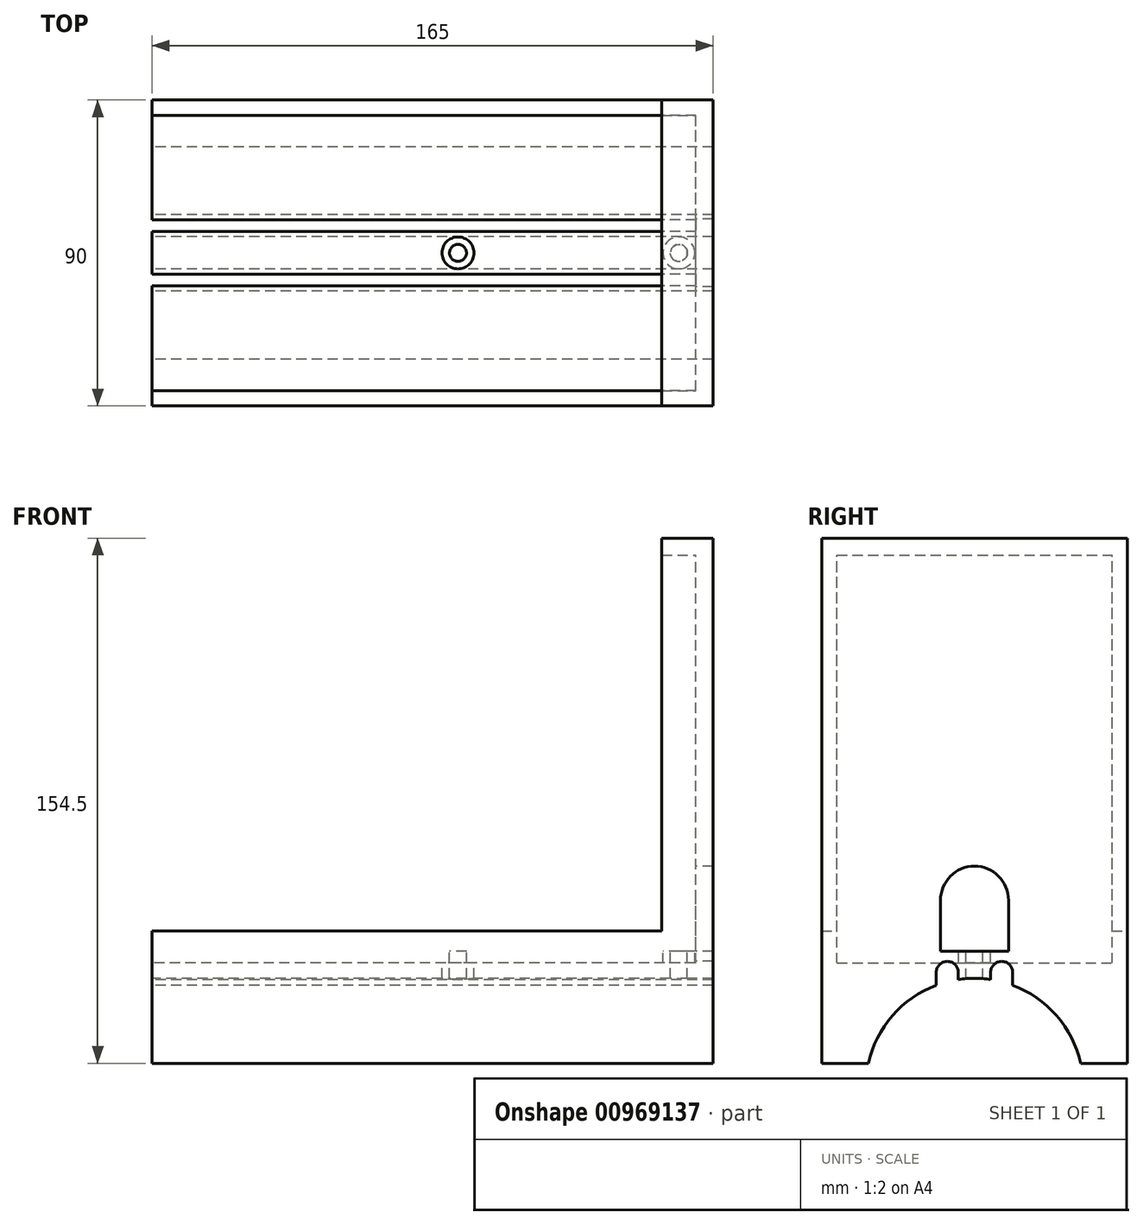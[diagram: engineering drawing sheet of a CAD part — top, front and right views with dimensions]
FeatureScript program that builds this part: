
annotation { "Feature Type Name" : "Feature", "Feature Type Description" : "" }
export const myFeature = defineFeature(function(context is Context, id is Id, definition is map)
    precondition{}
    {
        {
            var Q0;
            Q0=qCreatedBy(makeId("Right.planeOp"),FACE);
            var sketch = newSketch(context, id + "F0", { "sketchPlane" : qUnion([Q0])});
            skLineSegment(sketch, "E0", {"start": v(0, 25) * mm, "end": v(0, 89.87) * mm});
            skLineSegment(sketch, "E1", {"start": v(-31.25, 0) * mm, "end": v(-45, 0) * mm});
            skLineSegment(sketch, "E2.MirrorCS", {"start": v(31.25, 0) * mm, "end": v(45, 0) * mm});
            skArc(sketch, "E3", {"start": v(31.25, 0) * mm, "mid": v(24.15, 14) * mm, "end": v(11.25, 22.96) * mm});
            skPoint(sketch, "E4.orphan", {"position": v(0, 0) * mm});
            skLineSegment(sketch, "E5.0", {"start": v(11.25, 22.96) * mm, "end": v(11.25, 26.75) * mm});
            skLineSegment(sketch, "E6.MirrorCS", {"start": v(4.75, 24.65) * mm, "end": v(4.75, 26.75) * mm});
            skArc(sketch, "E7.trimOffspring", {"start": v(11.25, 26.75) * mm, "mid": v(8, 30) * mm, "end": v(4.75, 26.75) * mm});
            skArc(sketch, "E8.trimOffspring", {"start": v(4.75, 24.65) * mm, "mid": v(0, 25) * mm, "end": v(-4.75, 24.65) * mm});
            skLineSegment(sketch, "E9.MirrorCS", {"start": v(-4.75, 24.65) * mm, "end": v(-4.75, 26.75) * mm});
            skArc(sketch, "E10.MirrorCS", {"start": v(-11.25, 26.75) * mm, "mid": v(-8, 30) * mm, "end": v(-4.75, 26.75) * mm});
            skLineSegment(sketch, "E11.MirrorCS", {"start": v(-11.25, 22.96) * mm, "end": v(-11.25, 26.75) * mm});
            skArc(sketch, "E12.trimOffspring", {"start": v(-11.25, 22.96) * mm, "mid": v(-24.15, 14) * mm, "end": v(-31.25, 0) * mm});
            skPoint(sketch, "E13.orphan", {"position": v(-31.25, 89.87) * mm});
            skPoint(sketch, "E14.orphan", {"position": v(31.25, 89.87) * mm});
            skPoint(sketch, "E15.orphan", {"position": v(-123.78, 0) * mm});
            skPoint(sketch, "E16.orphan", {"position": v(123.78, 0) * mm});
            skLineSegment(sketch, "E17.0", {"start": v(-45, 0) * mm, "end": v(-45, 39) * mm});
            skLineSegment(sketch, "E18.0", {"start": v(45, 0) * mm, "end": v(45, 39) * mm});
            skLineSegment(sketch, "E19.0", {"start": v(-45, 39) * mm, "end": v(-40.5, 39) * mm});
            skLineSegment(sketch, "E20.0", {"start": v(-40.5, 33) * mm, "end": v(-40.5, 39) * mm});
            skLineSegment(sketch, "E21.trimOffspring", {"start": v(0, 33) * mm, "end": v(40.5, 33) * mm});
            skLineSegment(sketch, "E22", {"start": v(-40.5, 33) * mm, "end": v(0, 33) * mm});
            skLineSegment(sketch, "E23.trimOffspring", {"start": v(40.5, 39) * mm, "end": v(45, 39) * mm});
            skLineSegment(sketch, "E24.MirrorCS", {"start": v(40.5, 33) * mm, "end": v(40.5, 39) * mm});
            skSolve(sketch);
        }
        {
            var Q0;
            Q0 = qSketchRegion(id + "F0", true);
            extrude(context, id + "F1", {"entities" : qUnion([Q0]), "depth" : 160 * mm, "offsetDistance" : 25 * mm});
        }
        {
            var Q0;
            Q0=makeQuery(id+"F1.opExtrude","CAP_FACE",FACE,{"disambiguationData":[OSD([sQuery(id+"F0.wireOp",EDGE,"E1"),sQuery(id+"F0.wireOp",EDGE,"E2.MirrorCS"),sQuery(id+"F0.wireOp",EDGE,"E3"),sQuery(id+"F0.wireOp",EDGE,"E5.0"),sQuery(id+"F0.wireOp",EDGE,"E6.MirrorCS"),sQuery(id+"F0.wireOp",EDGE,"E7.trimOffspring"),sQuery(id+"F0.wireOp",EDGE,"E8.trimOffspring"),sQuery(id+"F0.wireOp",EDGE,"E9.MirrorCS"),sQuery(id+"F0.wireOp",EDGE,"E10.MirrorCS"),sQuery(id+"F0.wireOp",EDGE,"E11.MirrorCS"),sQuery(id+"F0.wireOp",EDGE,"E12.trimOffspring"),sQuery(id+"F0.wireOp",EDGE,"E17.0"),sQuery(id+"F0.wireOp",EDGE,"E18.0"),sQuery(id+"F0.wireOp",EDGE,"E19.0"),sQuery(id+"F0.wireOp",EDGE,"E20.0"),sQuery(id+"F0.wireOp",EDGE,"E21.trimOffspring"),sQuery(id+"F0.wireOp",EDGE,"E22"),sQuery(id+"F0.wireOp",EDGE,"E23.trimOffspring"),sQuery(id+"F0.wireOp",EDGE,"E24.MirrorCS")])],"isStart":false});
            var sketch = newSketch(context, id + "F2", { "sketchPlane" : qUnion([Q0])});
            skLineSegment(sketch, "E25.0.5", {"start": v(31.25, 0) * mm, "end": v(45, 0) * mm});
            skLineSegment(sketch, "E25.0.6", {"start": v(45, 0) * mm, "end": v(45, 149.5) * mm});
            skLineSegment(sketch, "E25.0.12", {"start": v(-45, 149.5) * mm, "end": v(-45, 0) * mm});
            skLineSegment(sketch, "E25.0.13", {"start": v(-45, 0) * mm, "end": v(-31.25, 0) * mm});
            skLineSegment(sketch, "E26.0", {"start": v(-45, 149.5) * mm, "end": v(45, 149.5) * mm});
            skPoint(sketch, "E27.orphan", {"position": v(-45, 39) * mm});
            skPoint(sketch, "E28.orphan", {"position": v(45, 39) * mm});
            skArc(sketch, "E29.0.0", {"start": v(-4.75, 24.65) * mm, "mid": v(0, 25) * mm, "end": v(4.75, 24.65) * mm});
            skLineSegment(sketch, "E29.0.1", {"start": v(4.75, 24.65) * mm, "end": v(4.75, 26.75) * mm});
            skArc(sketch, "E29.0.2", {"start": v(4.75, 26.75) * mm, "mid": v(8, 30) * mm, "end": v(11.25, 26.75) * mm});
            skLineSegment(sketch, "E29.0.3", {"start": v(11.25, 26.75) * mm, "end": v(11.25, 22.96) * mm});
            skArc(sketch, "E29.0.4", {"start": v(11.25, 22.96) * mm, "mid": v(24.15, 14) * mm, "end": v(31.25, 0) * mm});
            skLineSegment(sketch, "E29.0.6", {"start": v(45, 0) * mm, "end": v(45, 39) * mm});
            skLineSegment(sketch, "E29.0.7", {"start": v(45, 39) * mm, "end": v(40.5, 39) * mm});
            skLineSegment(sketch, "E29.0.8", {"start": v(40.5, 39) * mm, "end": v(40.5, 33) * mm});
            skLineSegment(sketch, "E29.0.9", {"start": v(40.5, 33) * mm, "end": v(-40.5, 33) * mm});
            skLineSegment(sketch, "E29.0.10", {"start": v(-40.5, 33) * mm, "end": v(-40.5, 39) * mm});
            skLineSegment(sketch, "E29.0.11", {"start": v(-40.5, 39) * mm, "end": v(-45, 39) * mm});
            skLineSegment(sketch, "E29.0.12", {"start": v(-45, 39) * mm, "end": v(-45, 0) * mm});
            skArc(sketch, "E29.0.14", {"start": v(-31.25, 0) * mm, "mid": v(-24.15, 14) * mm, "end": v(-11.25, 22.96) * mm});
            skLineSegment(sketch, "E29.0.15", {"start": v(-11.25, 22.96) * mm, "end": v(-11.25, 26.75) * mm});
            skArc(sketch, "E29.0.16", {"start": v(-11.25, 26.75) * mm, "mid": v(-8, 30) * mm, "end": v(-4.75, 26.75) * mm});
            skLineSegment(sketch, "E29.0.17", {"start": v(-4.75, 26.75) * mm, "end": v(-4.75, 24.65) * mm});
            skSolve(sketch);
        }
        {
            var Q0;
            Q0 = qSketchRegion(id + "F2", true);
            extrude(context, id + "F3", {"entities" : qUnion([Q0]), "operationType" : NewBodyOperationType.ADD, "depth" : 5 * mm, "offsetDistance" : 25 * mm});
        }
        {
            var Q0;
            {var subQ0=sQuery(id+"F2.wireOp",EDGE,"E25.0.12");var subQ1=sQuery(id+"F2.wireOp",EDGE,"E25.0.6");var subQ2=sQuery(id+"F2.wireOp",EDGE,"E26.0");Q0=makeQuery(id+"F3.boolean.opBoolean","SPLIT",FACE,{"disambiguationData":[TD([makeQuery(id+"F1.opExtrude","SWEPT_FACE",FACE,{"disambiguationData":[OSD([sQuery(id+"F0.wireOp",EDGE,"E17.0")])]})])],"derivedFrom":makeQuery(id+"F3.opExtrude","CAP_FACE",FACE,{"disambiguationData":[OSD([sQuery(id+"F2.wireOp",EDGE,"E25.0.5"),subQ1,subQ0,sQuery(id+"F2.wireOp",EDGE,"E25.0.13"),subQ2])],"isStart":true})});}
            var sketch = newSketch(context, id + "F4", { "sketchPlane" : qUnion([Q0])});
            skLineSegment(sketch, "E30.0", {"start": v(-40.5, 39) * mm, "end": v(-45, 39) * mm});
            skLineSegment(sketch, "E31", {"start": v(-45, 39) * mm, "end": v(-45, 149.5) * mm});
            skLineSegment(sketch, "E32", {"start": v(-40.5, 39) * mm, "end": v(-40.5, 149.5) * mm});
            skPoint(sketch, "E33.orphan", {"position": v(45, 149.5) * mm});
            skLineSegment(sketch, "E34.0", {"start": v(45, 39) * mm, "end": v(40.5, 39) * mm});
            skLineSegment(sketch, "E35.0", {"start": v(45, 149.5) * mm, "end": v(45, 39) * mm});
            skLineSegment(sketch, "E36", {"start": v(40.5, 39) * mm, "end": v(40.5, 149.5) * mm});
            skLineSegment(sketch, "E37.0", {"start": v(-40.5, 149.5) * mm, "end": v(-45, 149.5) * mm});
            skLineSegment(sketch, "E38.0", {"start": v(45, 149.5) * mm, "end": v(40.5, 149.5) * mm});
            skPoint(sketch, "E39.orphan", {"position": v(-45, 149.5) * mm});
            skSolve(sketch);
        }
        {
            var Q0;
            Q0 = qSketchRegion(id + "F4", true);
            extrude(context, id + "F5", {"entities" : qUnion([Q0]), "operationType" : NewBodyOperationType.ADD, "depth" : 10 * mm, "offsetDistance" : 25 * mm});
        }
        {
            var Q0;
            Q0=makeQuery(id+"F5.boolean.opBoolean","MERGE",FACE,{"derivedFrom":[makeQuery(id+"F3.opExtrude","SWEPT_FACE",FACE,{"disambiguationData":[OSD([sQuery(id+"F2.wireOp",EDGE,"E26.0")])]}),makeQuery(id+"F5.opExtrude","SWEPT_FACE",FACE,{"disambiguationData":[OSD([sQuery(id+"F4.wireOp",EDGE,"E37.0")])]}),makeQuery(id+"F5.opExtrude","SWEPT_FACE",FACE,{"disambiguationData":[OSD([sQuery(id+"F4.wireOp",EDGE,"E38.0")])]})]});
            var sketch = newSketch(context, id + "F6", { "sketchPlane" : qUnion([Q0])});
            skLineSegment(sketch, "E40.0.3", {"start": v(150, -45) * mm, "end": v(165, -45) * mm});
            skLineSegment(sketch, "E40.0.4", {"start": v(165, -45) * mm, "end": v(165, 45) * mm});
            skLineSegment(sketch, "E40.0.5", {"start": v(165, 45) * mm, "end": v(150, 45) * mm});
            skLineSegment(sketch, "E40.0.6", {"start": v(150, 45) * mm, "end": v(150, -45) * mm});
            skPoint(sketch, "E41.orphan", {"position": v(150, 40.5) * mm});
            skLineSegment(sketch, "E42.0", {"start": v(145, 45) * mm, "end": v(145, -45) * mm});
            skSolve(sketch);
        }
        {
            var Q0;
            Q0 = qSketchRegion(id + "F6", true);
            extrude(context, id + "F7", {"entities" : qUnion([Q0]), "operationType" : NewBodyOperationType.ADD, "depth" : 5 * mm, "offsetDistance" : 25 * mm});
        }
        {
            var Q0;
            Q0=makeQuery(id+"F1.opExtrude","SWEPT_FACE",FACE,{"disambiguationData":[OSD([sQuery(id+"F0.wireOp",EDGE,"E21.trimOffspring"),sQuery(id+"F0.wireOp",EDGE,"E22")])]});
            var sketch = newSketch(context, id + "F8", { "sketchPlane" : qUnion([Q0])});
            skLineSegment(sketch, "E43.0", {"start": v(160, -40.5) * mm, "end": v(160, 40.5) * mm});
            skLineSegment(sketch, "E44.0", {"start": v(155, -40.5) * mm, "end": v(155, 40.5) * mm});
            skCircle(sketch, "E45", {"center": v(155, 0) * mm, "radius": 2.5 * mm});
            skCircle(sketch, "E46", {"center": v(155, 0) * mm, "radius": 4.7 * mm});
            skLineSegment(sketch, "E47.0", {"start": v(122.5, -40.5) * mm, "end": v(122.5, 40.5) * mm});
            skCircle(sketch, "E48.MirrorC", {"center": v(90, 0) * mm, "radius": 4.7 * mm});
            skCircle(sketch, "E49.MirrorC", {"center": v(90, 0) * mm, "radius": 2.5 * mm});
            skSolve(sketch);
        }
        {
            var Q0;
            {var subQ0=sQuery(id+"F8.wireOp",EDGE,"E45");var subQ1=sQuery(id+"F8.wireOp",EDGE,"E44.0");var subQ2=makeQuery(id+"F8.imprint","INTERSECT",VERTEX,{"disambiguationData":[OD(0.0)],"derivedFrom":[subQ1,subQ0]});Q0=makeQuery(id+"F8.imprint","IMPRINT",FACE,{"disambiguationData":[TD([[makeQuery(id+"F8.imprint","IMPRINT",EDGE,{"disambiguationData":[TD([[subQ2,-1.0]])],"derivedFrom":subQ1}),-1.0]])]});}
            var Q1;
            {var subQ0=sQuery(id+"F8.wireOp",EDGE,"E45");var subQ1=sQuery(id+"F8.wireOp",EDGE,"E44.0");var subQ2=makeQuery(id+"F8.imprint","INTERSECT",VERTEX,{"disambiguationData":[OD(0.0)],"derivedFrom":[subQ1,subQ0]});Q1=makeQuery(id+"F8.imprint","IMPRINT",FACE,{"disambiguationData":[TD([[makeQuery(id+"F8.imprint","IMPRINT",EDGE,{"disambiguationData":[TD([[subQ2,-1.0]])],"derivedFrom":subQ1}),1.0]])]});}
            var Q2;
            Q2=makeQuery(id+"F8.imprint","IMPRINT",FACE,{"disambiguationData":[TD([[makeQuery(id+"F8.imprint","IMPRINT",EDGE,{"derivedFrom":sQuery(id+"F8.wireOp",EDGE,"E49.MirrorC")}),-1.0]])]});
            extrude(context, id + "F9", {"entities" : qUnion([Q0, Q1, Q2]), "operationType" : NewBodyOperationType.REMOVE, "endBound" : BoundingType.THROUGH_ALL, "oppositeDirection" : true, "depth" : 25 * mm, "offsetDistance" : 25 * mm});
        }
        {
            var Q0;
            {var subQ0=sQuery(id+"F8.wireOp",EDGE,"E46");var subQ1=sQuery(id+"F8.wireOp",EDGE,"E44.0");var subQ2=makeQuery(id+"F8.imprint","INTERSECT",VERTEX,{"disambiguationData":[OD(0.0)],"derivedFrom":[subQ1,subQ0]});Q0=makeQuery(id+"F8.imprint","IMPRINT",FACE,{"disambiguationData":[TD([[makeQuery(id+"F8.imprint","IMPRINT",EDGE,{"disambiguationData":[TD([[subQ2,-1.0]])],"derivedFrom":subQ1}),1.0]])]});}
            var Q1;
            {var subQ0=sQuery(id+"F8.wireOp",EDGE,"E46");var subQ1=sQuery(id+"F8.wireOp",EDGE,"E44.0");var subQ2=makeQuery(id+"F8.imprint","INTERSECT",VERTEX,{"disambiguationData":[OD(0.0)],"derivedFrom":[subQ1,subQ0]});Q1=makeQuery(id+"F8.imprint","IMPRINT",FACE,{"disambiguationData":[TD([[makeQuery(id+"F8.imprint","IMPRINT",EDGE,{"disambiguationData":[TD([[subQ2,-1.0]])],"derivedFrom":subQ1}),-1.0]])]});}
            var Q2;
            Q2=makeQuery(id+"F8.imprint","IMPRINT",FACE,{"disambiguationData":[TD([[makeQuery(id+"F8.imprint","IMPRINT",EDGE,{"derivedFrom":sQuery(id+"F8.wireOp",EDGE,"E48.MirrorC")}),-1.0]])]});
            extrude(context, id + "F10", {"entities" : qUnion([Q0, Q1, Q2]), "operationType" : NewBodyOperationType.REMOVE, "oppositeDirection" : true, "depth" : 3.5 * mm, "offsetDistance" : 25 * mm});
        }
        {
            var Q0;
            Q0=makeQuery(id+"F3.opExtrude","CAP_FACE",FACE,{"disambiguationData":[OSD([sQuery(id+"F2.wireOp",EDGE,"E25.0.6"),sQuery(id+"F2.wireOp",EDGE,"E25.0.12"),sQuery(id+"F2.wireOp",EDGE,"E26.0"),sQuery(id+"F2.wireOp",EDGE,"E29.0.0"),sQuery(id+"F2.wireOp",EDGE,"E29.0.1"),sQuery(id+"F2.wireOp",EDGE,"E29.0.2"),sQuery(id+"F2.wireOp",EDGE,"E29.0.3"),sQuery(id+"F2.wireOp",EDGE,"E29.0.4"),sQuery(id+"F2.wireOp",EDGE,"E25.0.5"),sQuery(id+"F2.wireOp",EDGE,"E29.0.6"),sQuery(id+"F2.wireOp",EDGE,"E29.0.12"),sQuery(id+"F2.wireOp",EDGE,"E25.0.13"),sQuery(id+"F2.wireOp",EDGE,"E29.0.14"),sQuery(id+"F2.wireOp",EDGE,"E29.0.15"),sQuery(id+"F2.wireOp",EDGE,"E29.0.16"),sQuery(id+"F2.wireOp",EDGE,"E29.0.17")])],"isStart":true});
            var sketch = newSketch(context, id + "F11", { "sketchPlane" : qUnion([Q0])});
            skLineSegment(sketch, "E50.0", {"start": v(40.5, 33) * mm, "end": v(-40.5, 33) * mm});
            skLineSegment(sketch, "E51.0", {"start": v(40.5, 58) * mm, "end": v(-40.5, 58) * mm});
            skLineSegment(sketch, "E52", {"start": v(0, 33) * mm, "end": v(0, 72.72) * mm});
            skLineSegment(sketch, "E53.0", {"start": v(10, 33) * mm, "end": v(10, 72.72) * mm});
            skLineSegment(sketch, "E54.0", {"start": v(-10, 33) * mm, "end": v(-10, 48) * mm});
            skLineSegment(sketch, "E55.0", {"start": v(40.5, 48) * mm, "end": v(-40.5, 48) * mm});
            skArc(sketch, "E56", {"start": v(10, 48) * mm, "mid": v(0, 58) * mm, "end": v(-10, 48) * mm});
            skLineSegment(sketch, "E57.trimOffspring", {"start": v(-10, 58) * mm, "end": v(-10, 72.72) * mm});
            skSolve(sketch);
        }
        {
            var Q0;
            {var subQ0=sQuery(id+"F11.wireOp",EDGE,"E52");var subQ1=sQuery(id+"F11.wireOp",EDGE,"E50.0");var subQ2=makeQuery(id+"F11.imprint","INTERSECT",VERTEX,{"derivedFrom":[subQ1,subQ0]});Q0=makeQuery(id+"F11.imprint","IMPRINT",FACE,{"disambiguationData":[TD([[makeQuery(id+"F11.imprint","IMPRINT",EDGE,{"disambiguationData":[TD([[subQ2,1.0]])],"derivedFrom":subQ1}),-1.0]])]});}
            var Q1;
            {var subQ3=sQuery(id+"F11.wireOp",EDGE,"E54.0");Q1=makeQuery(id+"F11.imprint","IMPRINT",FACE,{"disambiguationData":[TD([[makeQuery(id+"F11.imprint","IMPRINT",EDGE,{"derivedFrom":subQ3}),-1.0]])]});}
            var Q2;
            {var subQ0=sQuery(id+"F11.wireOp",EDGE,"E55.0");var subQ1=sQuery(id+"F11.wireOp",EDGE,"E52");var subQ2=makeQuery(id+"F11.imprint","INTERSECT",VERTEX,{"derivedFrom":[subQ1,subQ0]});Q2=makeQuery(id+"F11.imprint","IMPRINT",FACE,{"disambiguationData":[TD([[makeQuery(id+"F11.imprint","IMPRINT",EDGE,{"disambiguationData":[TD([[subQ2,-1.0]])],"derivedFrom":subQ1}),-1.0]])]});}
            var Q3;
            {var subQ0=sQuery(id+"F11.wireOp",EDGE,"E55.0");var subQ1=sQuery(id+"F11.wireOp",EDGE,"E52");var subQ2=makeQuery(id+"F11.imprint","INTERSECT",VERTEX,{"derivedFrom":[subQ1,subQ0]});Q3=makeQuery(id+"F11.imprint","IMPRINT",FACE,{"disambiguationData":[TD([[makeQuery(id+"F11.imprint","IMPRINT",EDGE,{"disambiguationData":[TD([[subQ2,-1.0]])],"derivedFrom":subQ1}),1.0]])]});}
            extrude(context, id + "F12", {"entities" : qUnion([Q0, Q1, Q2, Q3]), "operationType" : NewBodyOperationType.REMOVE, "endBound" : BoundingType.THROUGH_ALL, "oppositeDirection" : true, "depth" : 25 * mm, "offsetDistance" : 25 * mm});
        }
    });
